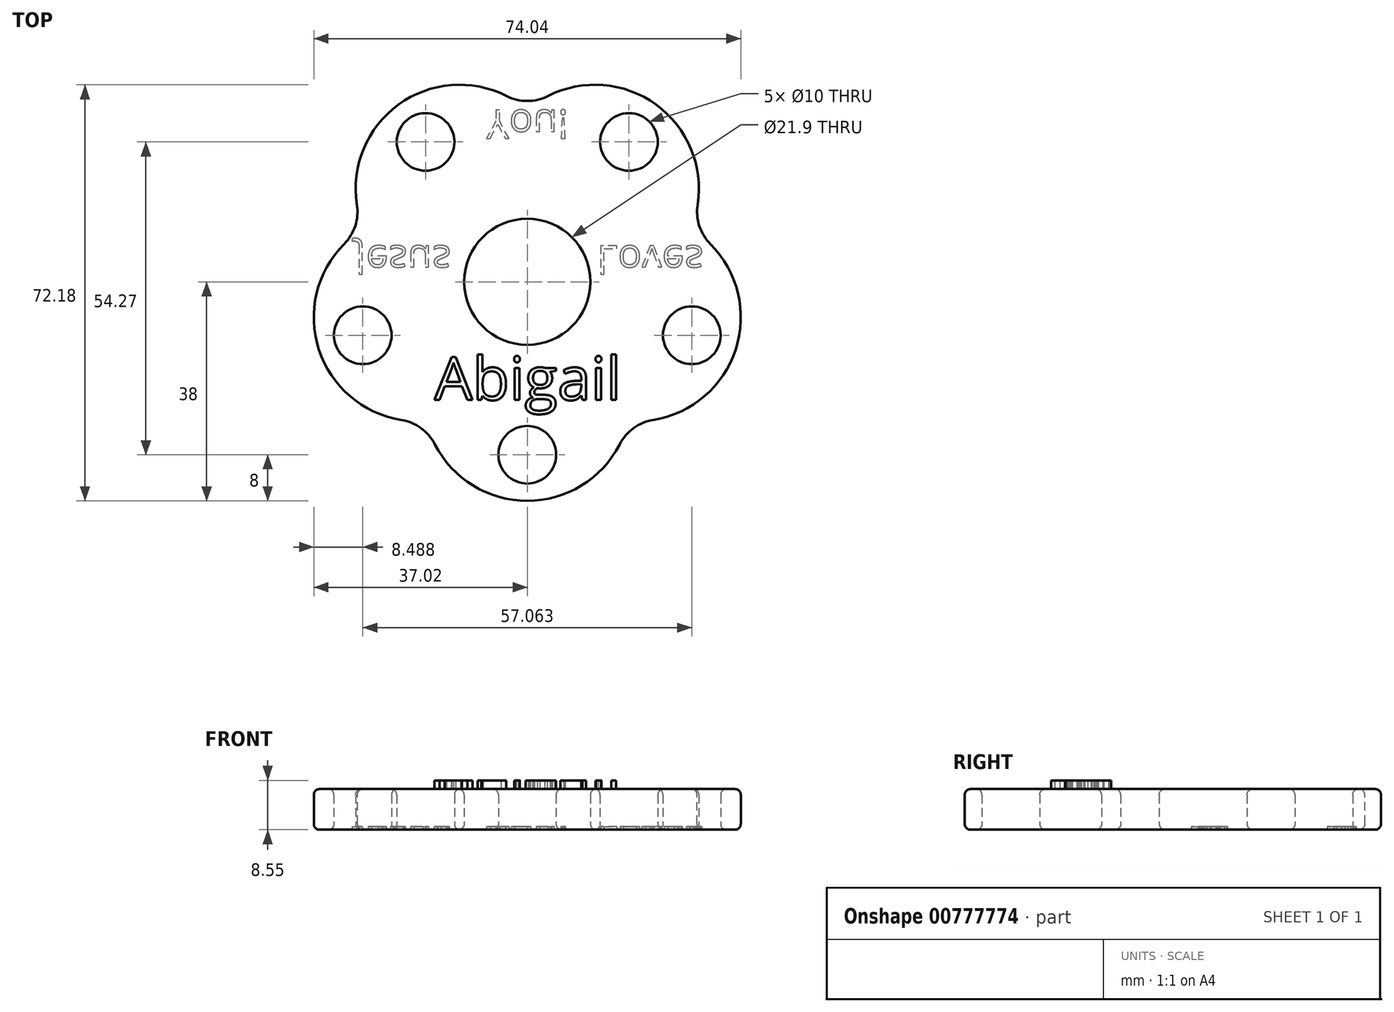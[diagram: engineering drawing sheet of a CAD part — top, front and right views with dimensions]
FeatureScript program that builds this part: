
annotation { "Feature Type Name" : "Feature", "Feature Type Description" : "" }
export const myFeature = defineFeature(function(context is Context, id is Id, definition is map)
    precondition{}
    {
        {
            var Q0;
            Q0=qCreatedBy(makeId("Top.planeOp"),FACE);
            var sketch = newSketch(context, id + "F0", { "sketchPlane" : qUnion([Q0])});
            skCircle(sketch, "E0.cCircle", {"center": v(0, 0) * mm, "radius": 20 * mm, "construction": true});
            skPoint(sketch, "E0.0.midPoint", {"position": v(11.76, 16.18) * mm});
            skArc(sketch, "E1", {"start": v(0, 29.81) * mm, "mid": v(-22.34, 30.74) * mm, "end": v(-28.35, 9.21) * mm});
            skArc(sketch, "E2", {"start": v(28.35, 9.21) * mm, "mid": v(22.34, 30.74) * mm, "end": v(0, 29.81) * mm});
            skArc(sketch, "E3", {"start": v(17.52, -24.12) * mm, "mid": v(36.14, -11.74) * mm, "end": v(28.35, 9.21) * mm});
            skArc(sketch, "E4", {"start": v(-17.52, -24.12) * mm, "mid": v(0, -38) * mm, "end": v(17.52, -24.12) * mm});
            skArc(sketch, "E5", {"start": v(-28.35, 9.21) * mm, "mid": v(-36.14, -11.74) * mm, "end": v(-17.52, -24.12) * mm});
            skCircle(sketch, "E6", {"center": v(0, 0) * mm, "radius": 29.81 * mm, "construction": true});
            skCircle(sketch, "E7", {"center": v(0, 0) * mm, "radius": 10.95 * mm});
            skCircle(sketch, "E8", {"center": v(-17.63, 24.27) * mm, "radius": 5 * mm});
            skCircle(sketch, "E9", {"center": v(17.63, 24.27) * mm, "radius": 5 * mm});
            skCircle(sketch, "E10", {"center": v(28.53, -9.27) * mm, "radius": 5 * mm});
            skCircle(sketch, "E11", {"center": v(0, -30) * mm, "radius": 5 * mm});
            skCircle(sketch, "E12", {"center": v(-28.53, -9.27) * mm, "radius": 5 * mm});
            skCircle(sketch, "E13", {"center": v(0, 0) * mm, "radius": 30 * mm, "construction": true});
            skLineSegment(sketch, "E14", {"start": v(0, 0) * mm, "end": v(0, 61.86) * mm, "construction": true});
            skLineSegment(sketch, "E15", {"start": v(0, 0) * mm, "end": v(35.53, 48.9) * mm, "construction": true});
            skLineSegment(sketch, "E16", {"start": v(0, 0) * mm, "end": v(71.25, -23.15) * mm, "construction": true});
            skLineSegment(sketch, "E17", {"start": v(0, 0) * mm, "end": v(0, -35) * mm, "construction": true});
            skLineSegment(sketch, "E18", {"start": v(0, 0) * mm, "end": v(-62.8, -20.4) * mm, "construction": true});
            skLineSegment(sketch, "E19", {"start": v(0, 0) * mm, "end": v(-32.19, 44.3) * mm, "construction": true});
            skSolve(sketch);
        }
        {
            var Q0;
            Q0 = qSketchRegion(id + "F0", true);
            extrude(context, id + "F1", {"entities" : qUnion([Q0]), "depth" : 7.05 * mm, "offsetDistance" : 25.4 * mm});
        }
        {
            var Q0;
            Q0=makeQuery(id+"F1.opExtrude","SWEPT_EDGE",EDGE,{"disambiguationData":[OSD([sQuery(id+"F0.wireOp",EDGE,"E3"),sQuery(id+"F0.wireOp",EDGE,"E4")])]});
            var Q1;
            Q1=makeQuery(id+"F1.opExtrude","SWEPT_EDGE",EDGE,{"disambiguationData":[OSD([sQuery(id+"F0.wireOp",EDGE,"E2"),sQuery(id+"F0.wireOp",EDGE,"E3")])]});
            var Q2;
            Q2=makeQuery(id+"F1.opExtrude","SWEPT_EDGE",EDGE,{"disambiguationData":[OSD([sQuery(id+"F0.wireOp",EDGE,"E1"),sQuery(id+"F0.wireOp",EDGE,"E2")])]});
            var Q3;
            Q3=makeQuery(id+"F1.opExtrude","SWEPT_EDGE",EDGE,{"disambiguationData":[OSD([sQuery(id+"F0.wireOp",EDGE,"E1"),sQuery(id+"F0.wireOp",EDGE,"E5")])]});
            var Q4;
            Q4=makeQuery(id+"F1.opExtrude","SWEPT_EDGE",EDGE,{"disambiguationData":[OSD([sQuery(id+"F0.wireOp",EDGE,"E4"),sQuery(id+"F0.wireOp",EDGE,"E5")])]});
            fillet(context, id + "F2", {"entities" : qUnion([Q0, Q1, Q2, Q3, Q4]), "radius" : 8 * mm, "tangentPropagation" : true, "allowEdgeOverflow" : false});
        }
        {
            var Q0;
            Q0=makeQuery(id+"F1.opExtrude","CAP_FACE",FACE,{"disambiguationData":[OSD([sQuery(id+"F0.wireOp",EDGE,"E1"),sQuery(id+"F0.wireOp",EDGE,"E2"),sQuery(id+"F0.wireOp",EDGE,"E3"),sQuery(id+"F0.wireOp",EDGE,"E4"),sQuery(id+"F0.wireOp",EDGE,"E5"),sQuery(id+"F0.wireOp",EDGE,"E7"),sQuery(id+"F0.wireOp",EDGE,"E8"),sQuery(id+"F0.wireOp",EDGE,"E9"),sQuery(id+"F0.wireOp",EDGE,"E10"),sQuery(id+"F0.wireOp",EDGE,"E11"),sQuery(id+"F0.wireOp",EDGE,"E12")])],"isStart":false});
            var Q1;
            Q1=makeQuery(id+"F1.opExtrude","CAP_FACE",FACE,{"disambiguationData":[OSD([sQuery(id+"F0.wireOp",EDGE,"E1"),sQuery(id+"F0.wireOp",EDGE,"E2"),sQuery(id+"F0.wireOp",EDGE,"E3"),sQuery(id+"F0.wireOp",EDGE,"E4"),sQuery(id+"F0.wireOp",EDGE,"E5"),sQuery(id+"F0.wireOp",EDGE,"E7"),sQuery(id+"F0.wireOp",EDGE,"E8"),sQuery(id+"F0.wireOp",EDGE,"E9"),sQuery(id+"F0.wireOp",EDGE,"E10"),sQuery(id+"F0.wireOp",EDGE,"E11"),sQuery(id+"F0.wireOp",EDGE,"E12")])],"isStart":true});
            fillet(context, id + "F3", {"entities" : qUnion([Q0, Q1]), "radius" : 1 * mm, "tangentPropagation" : true, "allowEdgeOverflow" : false});
        }
        {
            var Q0;
            Q0=makeQuery(id+"F1.opExtrude","CAP_FACE",FACE,{"disambiguationData":[OSD([sQuery(id+"F0.wireOp",EDGE,"E1"),sQuery(id+"F0.wireOp",EDGE,"E2"),sQuery(id+"F0.wireOp",EDGE,"E3"),sQuery(id+"F0.wireOp",EDGE,"E4"),sQuery(id+"F0.wireOp",EDGE,"E5"),sQuery(id+"F0.wireOp",EDGE,"E7"),sQuery(id+"F0.wireOp",EDGE,"E8"),sQuery(id+"F0.wireOp",EDGE,"E9"),sQuery(id+"F0.wireOp",EDGE,"E10"),sQuery(id+"F0.wireOp",EDGE,"E11"),sQuery(id+"F0.wireOp",EDGE,"E12")])],"isStart":false});
            var sketch = newSketch(context, id + "F4", { "sketchPlane" : qUnion([Q0])});
            skText(sketch, "E20", { "text": "Abigail\n", "fontName": "OpenSans-Regular.ttf"});
            const initialGuessF4  = {"E20": [-0.01608, -0.0205, 1, 0, 0.0075]};
            skSetInitialGuess(sketch, initialGuessF4);
            skSolve(sketch);
        }
        {
            var Q0;
            Q0 = qSketchRegion(id + "F4", true);
            extrude(context, id + "F5", {"entities" : qUnion([Q0]), "operationType" : NewBodyOperationType.ADD, "depth" : 1.5 * mm, "offsetDistance" : 25 * mm});
        }
        {
            var Q0;
            Q0=makeQuery(id+"F1.opExtrude","CAP_FACE",FACE,{"disambiguationData":[OSD([sQuery(id+"F0.wireOp",EDGE,"E1"),sQuery(id+"F0.wireOp",EDGE,"E2"),sQuery(id+"F0.wireOp",EDGE,"E3"),sQuery(id+"F0.wireOp",EDGE,"E4"),sQuery(id+"F0.wireOp",EDGE,"E5"),sQuery(id+"F0.wireOp",EDGE,"E7"),sQuery(id+"F0.wireOp",EDGE,"E8"),sQuery(id+"F0.wireOp",EDGE,"E9"),sQuery(id+"F0.wireOp",EDGE,"E10"),sQuery(id+"F0.wireOp",EDGE,"E11"),sQuery(id+"F0.wireOp",EDGE,"E12")])],"isStart":true});
            var sketch = newSketch(context, id + "F6", { "sketchPlane" : qUnion([Q0])});
            skText(sketch, "E21", { "text": "Jesus              Loves", "fontName": "OpenSans-Regular.ttf"});
            skText(sketch, "E22", { "text": "You!", "fontName": "OpenSans-Regular.ttf"});
            const initialGuessF6  = {"E21": [-0.02983, -0.00626, 1, 0, 0.005], "E22": [-0.00706, -0.0298, 1, 0, 0.005]};
            skSetInitialGuess(sketch, initialGuessF6);
            skSolve(sketch);
        }
        {
            var Q0;
            Q0 = qSketchRegion(id + "F6", true);
            extrude(context, id + "F7", {"entities" : qUnion([Q0]), "operationType" : NewBodyOperationType.REMOVE, "oppositeDirection" : true, "depth" : .5 * mm, "offsetDistance" : 25 * mm});
        }
    });
